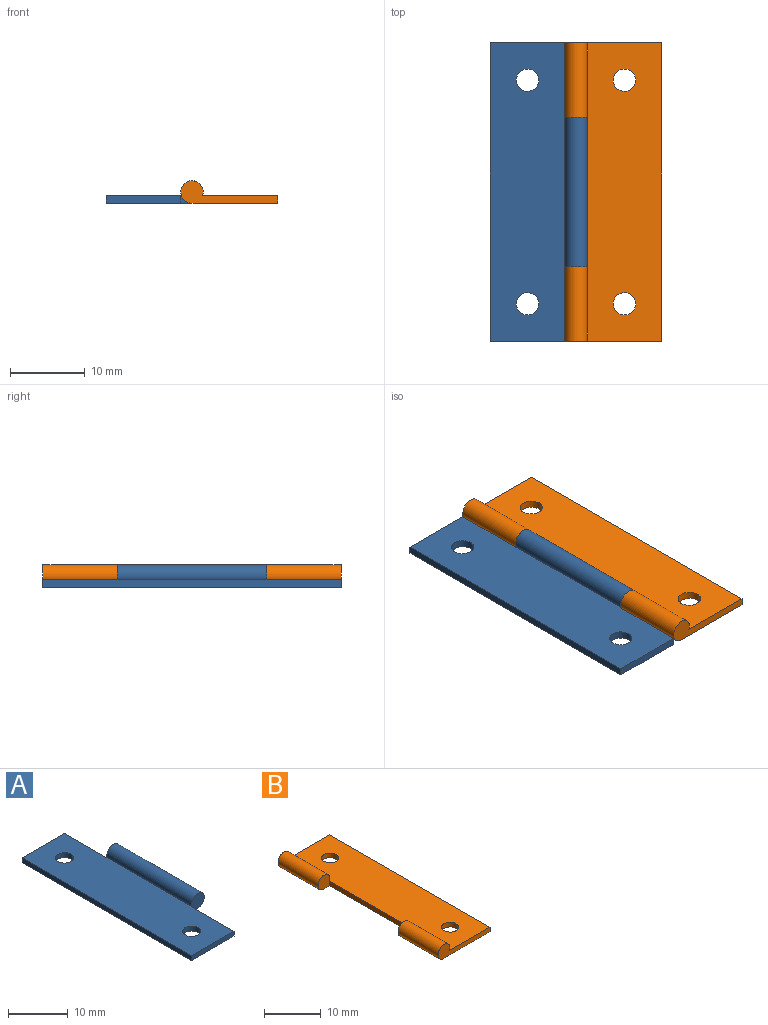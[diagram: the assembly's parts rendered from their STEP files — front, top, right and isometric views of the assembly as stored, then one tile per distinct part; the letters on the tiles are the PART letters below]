
ASSEMBLY  parts=2 mates=1
PART A: 12 faces, bbox 13x40x3 mm
  f0: plane 3x3mm, normal (0,1,0), area 7.5mm2, adj f1,f6,f10,f11
  f1: cylinder r=1.5mm len=20mm, axis (0,-1,0), area 151.6mm2, adj f0,f2,f10,f11
  f2: plane 3x3mm, normal (0,-1,0), area 7.5mm2, adj f1,f3,f10,f11
  f3: plane 10x1mm, normal (1,0,0), area 10mm2, adj f2,f8,f10,f11
  f4: plane 40x1mm, normal (-1,0,0), area 40mm2, adj f5,f8,f10,f11
  f5: plane 10x1mm, normal (0,1,0), area 10mm2, adj f4,f6,f10,f11
  f6: plane 10x1mm, normal (1,0,0), area 10mm2, adj f0,f5,f10,f11
  f7: cylinder r=1.5mm len=3mm, axis (0,0,-1), area 9.4mm2, adj f10,f11
  f8: plane 10x1mm, normal (0,-1,0), area 10mm2, adj f3,f4,f10,f11
  f9: cylinder r=1.5mm len=3mm, axis (0,0,-1), area 9.4mm2, adj f10,f11
  f10: plane 40x10.09mm, normal (0,0,1), area 387.6mm2, adj f0,f1,f2,f3,f4,f5,f6,f7
  f11: plane 40x11.5mm, normal (0,0,-1), area 415.9mm2, adj f0,f1,f2,f3,f4,f5,f6,f7
PART B: 12 faces, bbox 13x40x3 mm
  f0: plane 20x1mm, normal (-1,0,0), area 20mm2, adj f6,f7,f9,f11
  f1: plane 40x1mm, normal (1,0,0), area 40mm2, adj f2,f4,f6,f7
  f2: plane 13x3mm, normal (0,1,0), area 17.5mm2, adj f1,f6,f7,f8
  f3: cylinder r=1.5mm len=3mm, axis (0,0,-1), area 9.4mm2, adj f6,f7
  f4: plane 13x3mm, normal (0,-1,0), area 17.5mm2, adj f1,f6,f7,f10
  f5: cylinder r=1.5mm len=3mm, axis (0,0,-1), area 9.4mm2, adj f6,f7
  f6: plane 40x10.09mm, normal (0,0,1), area 387.6mm2, adj f0,f1,f2,f3,f4,f5,f8,f9
  f7: plane 40x11.5mm, normal (0,0,-1), area 415.9mm2, adj f0,f1,f2,f3,f4,f5,f8,f9
  f8: cylinder r=1.5mm len=10mm, axis (0,1,0), area 75.8mm2, adj f2,f6,f7,f9
  f9: plane 3x3mm, normal (0,-1,0), area 7.5mm2, adj f0,f6,f7,f8
  f10: cylinder r=1.5mm len=10mm, axis (0,-1,0), area 75.8mm2, adj f4,f6,f7,f11
  f11: plane 3x3mm, normal (0,1,0), area 7.5mm2, adj f0,f6,f7,f10
PLACE A rot(axis=(0,1,0.01),0deg) t=(5.83,-1.11,9.42)mm
PLACE B t=(5.83,-1.11,9.42)mm fixed
MATE revolute A.f1 <-> B.f8  axis (0,-1,0) through (4.33,-11.11,10.92)mm
